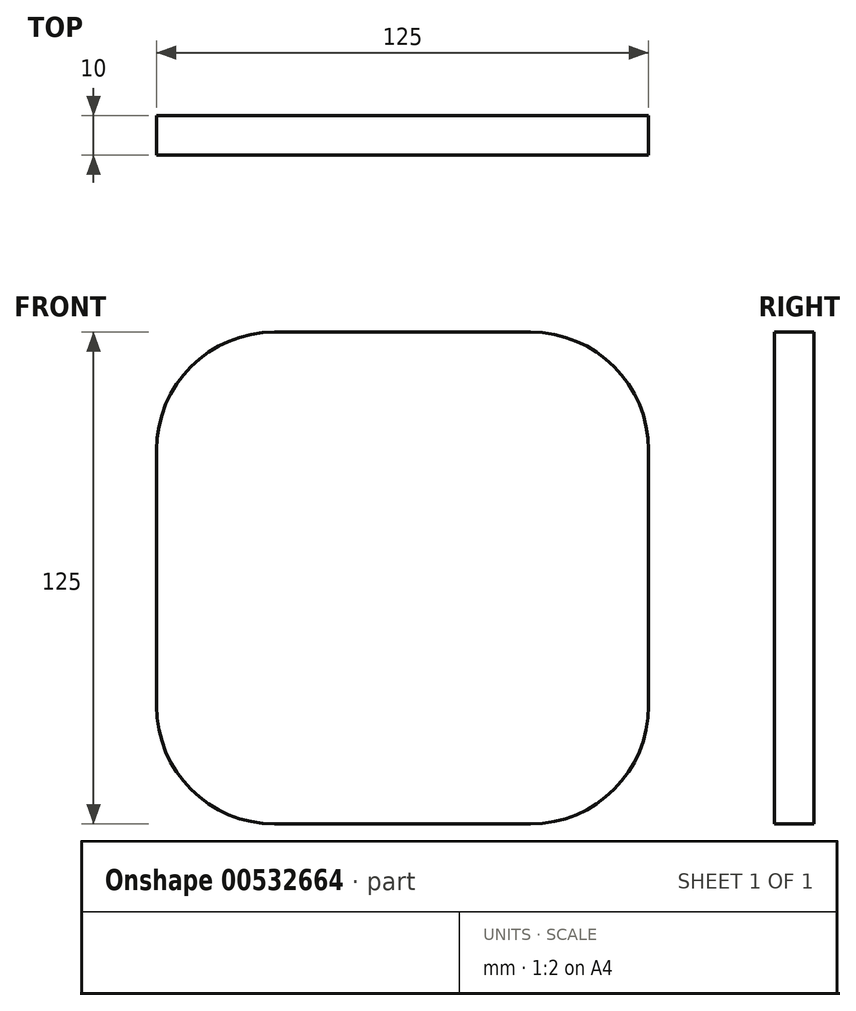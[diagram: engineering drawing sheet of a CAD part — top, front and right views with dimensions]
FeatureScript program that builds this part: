
annotation { "Feature Type Name" : "Feature", "Feature Type Description" : "" }
export const myFeature = defineFeature(function(context is Context, id is Id, definition is map)
    precondition{}
    {
        {
            var Q0;
            Q0=qCreatedBy(makeId("Front.planeOp"),FACE);
            var sketch = newSketch(context, id + "F0", { "sketchPlane" : qUnion([Q0])});
            skLineSegment(sketch, "E0.bottom", {"start": v(-32.5, 62.5) * mm, "end": v(32.5, 62.5) * mm});
            skLineSegment(sketch, "E0.top", {"start": v(-32.5, -62.5) * mm, "end": v(32.5, -62.5) * mm});
            skLineSegment(sketch, "E0.left", {"start": v(-62.5, 32.5) * mm, "end": v(-62.5, -32.5) * mm});
            skLineSegment(sketch, "E0.right", {"start": v(62.5, 32.5) * mm, "end": v(62.5, -32.5) * mm});
            skPoint(sketch, "E0.middle", {"position": v(0, 0) * mm});
            skPoint(sketch, "E1.visualSharp", {"position": v(-62.5, 62.5) * mm});
            skArc(sketch, "E1.filletArc", {"start": v(-32.5, 62.5) * mm, "mid": v(-53.71, 53.71) * mm, "end": v(-62.5, 32.5) * mm});
            skPoint(sketch, "E2.visualSharp", {"position": v(62.5, 62.5) * mm});
            skArc(sketch, "E2.filletArc", {"start": v(62.5, 32.5) * mm, "mid": v(53.71, 53.71) * mm, "end": v(32.5, 62.5) * mm});
            skPoint(sketch, "E3.visualSharp", {"position": v(62.5, -62.5) * mm});
            skArc(sketch, "E3.filletArc", {"start": v(32.5, -62.5) * mm, "mid": v(53.71, -53.71) * mm, "end": v(62.5, -32.5) * mm});
            skPoint(sketch, "E4.visualSharp", {"position": v(-62.5, -62.5) * mm});
            skArc(sketch, "E4.filletArc", {"start": v(-62.5, -32.5) * mm, "mid": v(-53.71, -53.71) * mm, "end": v(-32.5, -62.5) * mm});
            skSolve(sketch);
        }
        {
            var Q0;
            Q0=makeQuery(id+"F0.imprint","IMPRINT",FACE,{"disambiguationData":[TD([[makeQuery(id+"F0.imprint","IMPRINT",EDGE,{"derivedFrom":sQuery(id+"F0.wireOp",EDGE,"E0.bottom")}),-1.0]])]});
            extrude(context, id + "F1", {"entities" : qUnion([Q0]), "depth" : 10 * mm, "offsetDistance" : 25 * mm});
        }
    });
